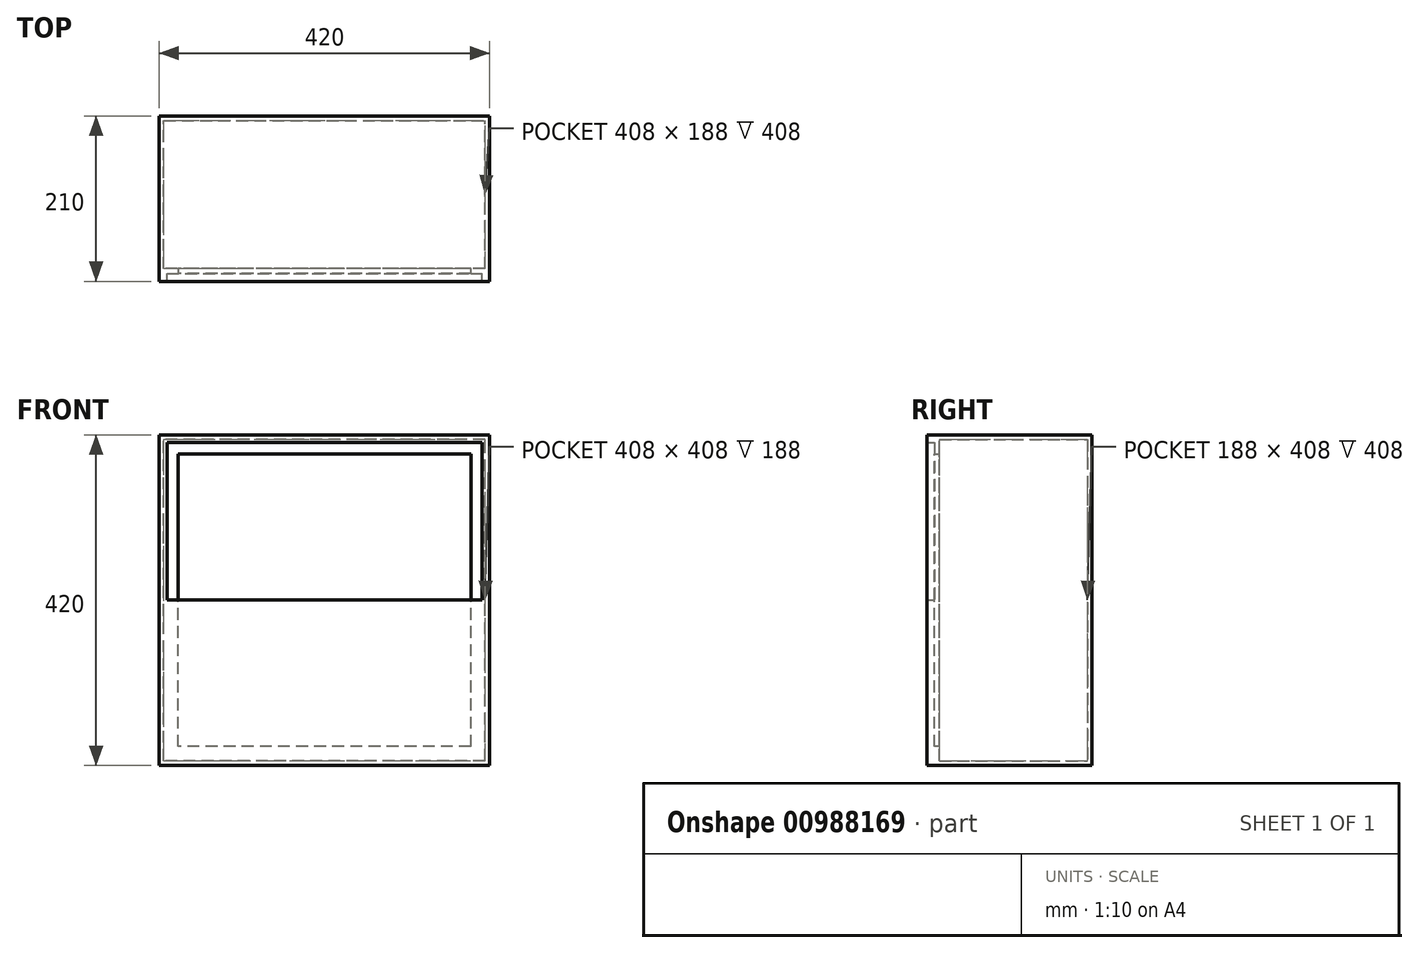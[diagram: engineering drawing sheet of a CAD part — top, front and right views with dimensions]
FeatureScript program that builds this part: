
annotation { "Feature Type Name" : "Feature", "Feature Type Description" : "" }
export const myFeature = defineFeature(function(context is Context, id is Id, definition is map)
    precondition{}
    {
        {
            var Q0;
            Q0=qCreatedBy(makeId("Front.planeOp"),FACE);
            var sketch = newSketch(context, id + "F0", { "sketchPlane" : qUnion([Q0])});
            skLineSegment(sketch, "E0.bottom", {"start": v(-210, 210) * mm, "end": v(210, 210) * mm});
            skLineSegment(sketch, "E0.top", {"start": v(-210, -210) * mm, "end": v(210, -210) * mm});
            skLineSegment(sketch, "E0.left", {"start": v(-210, 210) * mm, "end": v(-210, -210) * mm});
            skLineSegment(sketch, "E0.right", {"start": v(210, 210) * mm, "end": v(210, -210) * mm});
            skPoint(sketch, "E0.middle", {"position": v(0, 0) * mm});
            skSolve(sketch);
        }
        {
            var Q0;
            Q0 = qSketchRegion(id + "F0", true);
            extrude(context, id + "F1", {"entities" : qUnion([Q0]), "endBound" : BoundingType.SYMMETRIC, "depth" : 210 * mm, "offsetDistance" : 25.4 * mm});
        }
        {
            var Q0;
            Q0=makeQuery(id+"F1.opExtrude","CAP_FACE",FACE,{"disambiguationData":[OSD([sQuery(id+"F0.wireOp",EDGE,"E0.bottom"),sQuery(id+"F0.wireOp",EDGE,"E0.top"),sQuery(id+"F0.wireOp",EDGE,"E0.left"),sQuery(id+"F0.wireOp",EDGE,"E0.right")])],"isStart":false});
            shell(context, id + "F2", {"entities" : qUnion([Q0]), "thickness" : 6 * mm});
        }
        {
            var Q0;
            Q0=makeQuery(id+"F2.opShell","OFFSET_FACE",FACE,{"disambiguationData":[OSD([sQuery(id+"F0.wireOp",EDGE,"E0.left")])]});
            var sketch = newSketch(context, id + "F3", { "sketchPlane" : qUnion([Q0])});
            skLineSegment(sketch, "E1.top", {"start": v(-2, -194) * mm, "end": v(2, -194) * mm});
            skPoint(sketch, "E1.middle", {"position": v(0, 0) * mm});
            skLineSegment(sketch, "E2.bottom", {"start": v(-89, -204) * mm, "end": v(-95, -204) * mm});
            skLineSegment(sketch, "E2.top", {"start": v(-89, 204) * mm, "end": v(-95, 204) * mm});
            skLineSegment(sketch, "E2.left", {"start": v(-89, -204) * mm, "end": v(-89, 204) * mm});
            skLineSegment(sketch, "E2.right", {"start": v(-95, -204) * mm, "end": v(-95, 204) * mm});
            skPoint(sketch, "E2.middle", {"position": v(-92, 0) * mm});
            skSolve(sketch);
        }
        {
            var Q0;
            Q0 = qSketchRegion(id + "F3", true);
            extrude(context, id + "F4", {"entities" : qUnion([Q0]), "operationType" : NewBodyOperationType.ADD, "depth" : 18 * mm, "offsetDistance" : 25.4 * mm});
        }
        {
            var Q0;
            Q0=makeQuery(id+"F2.opShell","OFFSET_FACE",FACE,{"disambiguationData":[OSD([sQuery(id+"F0.wireOp",EDGE,"E0.right")])]});
            var sketch = newSketch(context, id + "F5", { "sketchPlane" : qUnion([Q0])});
            skLineSegment(sketch, "E3.bottom", {"start": v(95, -204) * mm, "end": v(89, -204) * mm});
            skLineSegment(sketch, "E3.top", {"start": v(95, 204) * mm, "end": v(89, 204) * mm});
            skLineSegment(sketch, "E3.left", {"start": v(89, -204) * mm, "end": v(89, 204) * mm});
            skLineSegment(sketch, "E3.right", {"start": v(95, -204) * mm, "end": v(95, 204) * mm});
            skPoint(sketch, "E3.middle", {"position": v(92, 0) * mm});
            skSolve(sketch);
        }
        {
            var Q0;
            Q0 = qSketchRegion(id + "F5", true);
            extrude(context, id + "F6", {"entities" : qUnion([Q0]), "operationType" : NewBodyOperationType.ADD, "depth" : 18 * mm, "offsetDistance" : 25.4 * mm});
        }
        {
            var Q0;
            Q0=makeQuery(id+"F4.opExtrude","CAP_FACE",FACE,{"disambiguationData":[OSD([sQuery(id+"F3.wireOp",EDGE,"E2.bottom"),sQuery(id+"F3.wireOp",EDGE,"E2.top"),sQuery(id+"F3.wireOp",EDGE,"E2.left"),sQuery(id+"F3.wireOp",EDGE,"E2.right")])],"isStart":false});
            var sketch = newSketch(context, id + "F7", { "sketchPlane" : qUnion([Q0])});
            skLineSegment(sketch, "E4.bottom", {"start": v(-95, 204) * mm, "end": v(-89, 204) * mm});
            skLineSegment(sketch, "E4.top", {"start": v(-95, 186) * mm, "end": v(-89, 186) * mm});
            skLineSegment(sketch, "E4.left", {"start": v(-95, 204) * mm, "end": v(-95, 186) * mm});
            skLineSegment(sketch, "E4.right", {"start": v(-89, 204) * mm, "end": v(-89, 186) * mm});
            skSolve(sketch);
        }
        {
            var Q0;
            Q0 = qSketchRegion(id + "F7", true);
            var Q1;
            Q1=makeQuery(id+"F6.opExtrude","CAP_FACE",FACE,{"disambiguationData":[OSD([sQuery(id+"F5.wireOp",EDGE,"E3.bottom"),sQuery(id+"F5.wireOp",EDGE,"E3.top"),sQuery(id+"F5.wireOp",EDGE,"E3.left"),sQuery(id+"F5.wireOp",EDGE,"E3.right")])],"isStart":false});
            extrude(context, id + "F8", {"entities" : qUnion([Q0]), "operationType" : NewBodyOperationType.ADD, "endBound" : BoundingType.UP_TO_SURFACE, "depth" : 12.2 * mm, "endBoundEntityFace" : qUnion([Q1]), "offsetDistance" : 25.4 * mm});
        }
        {
            var Q0;
            Q0=makeQuery(id+"F4.opExtrude","CAP_FACE",FACE,{"disambiguationData":[OSD([sQuery(id+"F3.wireOp",EDGE,"E2.bottom"),sQuery(id+"F3.wireOp",EDGE,"E2.top"),sQuery(id+"F3.wireOp",EDGE,"E2.left"),sQuery(id+"F3.wireOp",EDGE,"E2.right")])],"isStart":false});
            var sketch = newSketch(context, id + "F9", { "sketchPlane" : qUnion([Q0])});
            skLineSegment(sketch, "E5.bottom", {"start": v(-89, -204) * mm, "end": v(-95, -204) * mm});
            skLineSegment(sketch, "E5.top", {"start": v(-89, -186) * mm, "end": v(-95, -186) * mm});
            skLineSegment(sketch, "E5.left", {"start": v(-89, -204) * mm, "end": v(-89, -186) * mm});
            skLineSegment(sketch, "E5.right", {"start": v(-95, -204) * mm, "end": v(-95, -186) * mm});
            skSolve(sketch);
        }
        {
            var Q0;
            Q0 = qSketchRegion(id + "F9", true);
            var Q1;
            Q1=makeQuery(id+"F6.opExtrude","CAP_FACE",FACE,{"disambiguationData":[OSD([sQuery(id+"F5.wireOp",EDGE,"E3.bottom"),sQuery(id+"F5.wireOp",EDGE,"E3.top"),sQuery(id+"F5.wireOp",EDGE,"E3.left"),sQuery(id+"F5.wireOp",EDGE,"E3.right")])],"isStart":false});
            extrude(context, id + "F10", {"entities" : qUnion([Q0]), "operationType" : NewBodyOperationType.ADD, "endBound" : BoundingType.UP_TO_SURFACE, "depth" : 25.4 * mm, "endBoundEntityFace" : qUnion([Q1]), "offsetDistance" : 25.4 * mm});
        }
        {
            var Q0;
            Q0=makeQuery(id+"F10.boolean.opBoolean","MERGE",FACE,{"derivedFrom":[makeQuery(id+"F8.boolean.opBoolean","MERGE",FACE,{"derivedFrom":[makeQuery(id+"F4.opExtrude","SWEPT_FACE",FACE,{"disambiguationData":[OSD([sQuery(id+"F3.wireOp",EDGE,"E2.right")])]}),makeQuery(id+"F6.opExtrude","SWEPT_FACE",FACE,{"disambiguationData":[OSD([sQuery(id+"F5.wireOp",EDGE,"E3.right")])]}),makeQuery(id+"F8.opExtrude","SWEPT_FACE",FACE,{"disambiguationData":[OSD([sQuery(id+"F7.wireOp",EDGE,"E4.left")])]})]}),makeQuery(id+"F10.opExtrude","SWEPT_FACE",FACE,{"disambiguationData":[OSD([sQuery(id+"F9.wireOp",EDGE,"E5.right")])]})]});
            var sketch = newSketch(context, id + "F11", { "sketchPlane" : qUnion([Q0])});
            skLineSegment(sketch, "E6.bottom", {"start": v(-204, 204) * mm, "end": v(204, 204) * mm});
            skLineSegment(sketch, "E6.top", {"start": v(-204, -204) * mm, "end": v(204, -204) * mm});
            skLineSegment(sketch, "E6.left", {"start": v(-204, 204) * mm, "end": v(-204, -204) * mm});
            skLineSegment(sketch, "E6.right", {"start": v(204, 204) * mm, "end": v(204, -204) * mm});
            skPoint(sketch, "E6.middle", {"position": v(0, 0) * mm});
            skLineSegment(sketch, "E7.bottom", {"start": v(-200, 200) * mm, "end": v(200, 200) * mm});
            skLineSegment(sketch, "E7.top", {"start": v(-200, -200) * mm, "end": v(200, -200) * mm});
            skLineSegment(sketch, "E7.left", {"start": v(-200, 200) * mm, "end": v(-200, -200) * mm});
            skLineSegment(sketch, "E7.right", {"start": v(200, 200) * mm, "end": v(200, -200) * mm});
            skSolve(sketch);
        }
        {
            var Q0;
            Q0 = qSketchRegion(id + "F11", true);
            extrude(context, id + "F12", {"entities" : qUnion([Q0]), "operationType" : NewBodyOperationType.ADD, "depth" : 10 * mm, "offsetDistance" : 25.4 * mm});
        }
        {
            var Q0;
            Q0=makeQuery(id+"F10.boolean.opBoolean","MERGE",FACE,{"derivedFrom":[makeQuery(id+"F8.boolean.opBoolean","MERGE",FACE,{"derivedFrom":[makeQuery(id+"F4.opExtrude","SWEPT_FACE",FACE,{"disambiguationData":[OSD([sQuery(id+"F3.wireOp",EDGE,"E2.right")])]}),makeQuery(id+"F6.opExtrude","SWEPT_FACE",FACE,{"disambiguationData":[OSD([sQuery(id+"F5.wireOp",EDGE,"E3.right")])]}),makeQuery(id+"F8.opExtrude","SWEPT_FACE",FACE,{"disambiguationData":[OSD([sQuery(id+"F7.wireOp",EDGE,"E4.left")])]})]}),makeQuery(id+"F10.opExtrude","SWEPT_FACE",FACE,{"disambiguationData":[OSD([sQuery(id+"F9.wireOp",EDGE,"E5.right")])]})]});
            var sketch = newSketch(context, id + "F13", { "sketchPlane" : qUnion([Q0])});
            skLineSegment(sketch, "E8.bottom", {"start": v(-200, -200) * mm, "end": v(200, -200) * mm});
            skLineSegment(sketch, "E8.top", {"start": v(-200, 0) * mm, "end": v(200, 0) * mm});
            skLineSegment(sketch, "E8.left", {"start": v(-200, -200) * mm, "end": v(-200, 0) * mm});
            skLineSegment(sketch, "E8.right", {"start": v(200, -200) * mm, "end": v(200, 0) * mm});
            skSolve(sketch);
        }
        {
            var Q0;
            Q0 = qSketchRegion(id + "F13", true);
            extrude(context, id + "F14", {"entities" : qUnion([Q0]), "operationType" : NewBodyOperationType.ADD, "depth" : 10 * mm, "offsetDistance" : 25.4 * mm});
        }
    });
